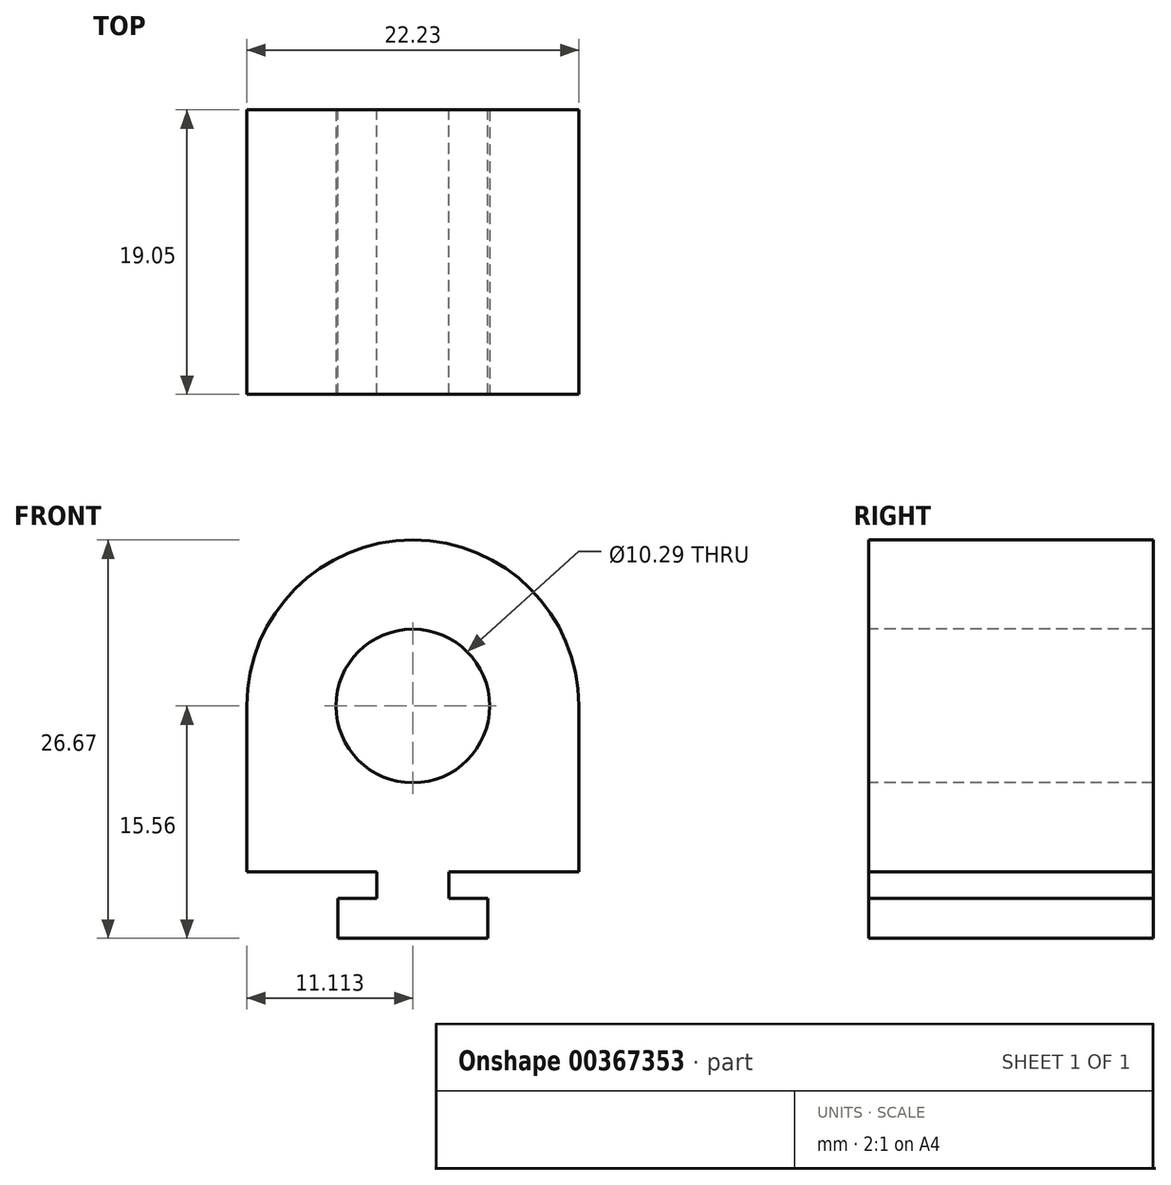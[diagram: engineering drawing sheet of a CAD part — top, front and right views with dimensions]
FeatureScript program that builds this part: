
annotation { "Feature Type Name" : "Feature", "Feature Type Description" : "" }
export const myFeature = defineFeature(function(context is Context, id is Id, definition is map)
    precondition{}
    {
        {
            var Q0;
            Q0=qCreatedBy(makeId("Front.planeOp"),FACE);
            var sketch = newSketch(context, id + "F0", { "sketchPlane" : qUnion([Q0])});
            skLineSegment(sketch, "E0", {"start": v(0, 0) * mm, "end": v(22.22, 0) * mm});
            skLineSegment(sketch, "E1", {"start": v(22.23, 0) * mm, "end": v(22.23, -4.76) * mm});
            skLineSegment(sketch, "E2", {"start": v(22.22, -4.76) * mm, "end": v(13.53, -4.76) * mm});
            skLineSegment(sketch, "E3", {"start": v(13.53, -4.76) * mm, "end": v(13.53, -6.54) * mm});
            skLineSegment(sketch, "E4", {"start": v(13.53, -6.54) * mm, "end": v(16.13, -6.54) * mm});
            skLineSegment(sketch, "E5", {"start": v(16.13, -6.54) * mm, "end": v(16.13, -9.2) * mm});
            skLineSegment(sketch, "E6", {"start": v(16.13, -9.2) * mm, "end": v(6.1, -9.2) * mm});
            skLineSegment(sketch, "E7", {"start": v(6.1, -9.2) * mm, "end": v(6.1, -6.54) * mm});
            skLineSegment(sketch, "E8", {"start": v(6.1, -6.54) * mm, "end": v(8.7, -6.54) * mm});
            skLineSegment(sketch, "E9", {"start": v(8.7, -6.54) * mm, "end": v(8.7, -4.76) * mm});
            skLineSegment(sketch, "E10", {"start": v(8.7, -4.76) * mm, "end": v(0, -4.76) * mm});
            skLineSegment(sketch, "E11", {"start": v(0, -4.76) * mm, "end": v(0, 0) * mm});
            skSolve(sketch);
        }
        {
            var Q0;
            Q0=makeQuery(id+"F0.imprint","IMPRINT",FACE,{"disambiguationData":[TD([[makeQuery(id+"F0.imprint","IMPRINT",EDGE,{"derivedFrom":sQuery(id+"F0.wireOp",EDGE,"E0")}),-1.0]])]});
            extrude(context, id + "F1", {"entities" : qUnion([Q0]), "depth" : 6.35 * mm});
        }
        {
            var Q0;
            Q0=makeQuery(id+"F1.opExtrude","CAP_FACE",FACE,{"disambiguationData":[OSD([sQuery(id+"F0.wireOp",EDGE,"E0"),sQuery(id+"F0.wireOp",EDGE,"E1"),sQuery(id+"F0.wireOp",EDGE,"E2"),sQuery(id+"F0.wireOp",EDGE,"E3"),sQuery(id+"F0.wireOp",EDGE,"E4"),sQuery(id+"F0.wireOp",EDGE,"E5"),sQuery(id+"F0.wireOp",EDGE,"E6"),sQuery(id+"F0.wireOp",EDGE,"E7"),sQuery(id+"F0.wireOp",EDGE,"E8"),sQuery(id+"F0.wireOp",EDGE,"E9"),sQuery(id+"F0.wireOp",EDGE,"E10"),sQuery(id+"F0.wireOp",EDGE,"E11")])],"isStart":false});
            var sketch = newSketch(context, id + "F2", { "sketchPlane" : qUnion([Q0])});
            skLineSegment(sketch, "E12", {"start": v(0, -4.76) * mm, "end": v(0, 6.35) * mm});
            skLineSegment(sketch, "E13", {"start": v(22.23, -4.76) * mm, "end": v(22.23, 6.35) * mm});
            skArc(sketch, "E14", {"start": v(22.23, 6.35) * mm, "mid": v(11.11, 17.46) * mm, "end": v(0, 6.35) * mm});
            skCircle(sketch, "E15", {"center": v(11.11, 6.35) * mm, "radius": 5.14 * mm});
            skCircle(sketch, "E16", {"center": v(11.11, 6.35) * mm, "radius": 4.76 * mm, "construction": true});
            skSolve(sketch);
        }
        {
            var Q0;
            {var subQ0=sQuery(id+"F2.wireOp",EDGE,"E14");Q0=makeQuery(id+"F2.imprint","IMPRINT",FACE,{"disambiguationData":[TD([[makeQuery(id+"F2.imprint","IMPRINT",EDGE,{"derivedFrom":subQ0}),1.0]])]});}
            var Q1;
            {var subQ1=makeQuery(id+"F1.opExtrude","CAP_EDGE",EDGE,{"disambiguationData":[OSD([sQuery(id+"F0.wireOp",EDGE,"E0")])],"isStart":false});Q1=makeQuery(id+"F2.imprint","IMPRINT",FACE,{"disambiguationData":[TD([[makeQuery(id+"F2.imprint","IMPRINT",EDGE,{"derivedFrom":subQ1}),-1.0]])]});}
            extrude(context, id + "F3", {"entities" : qUnion([Q0, Q1]), "operationType" : NewBodyOperationType.ADD, "oppositeDirection" : true, "depth" : 19.05 * mm});
        }
    });
